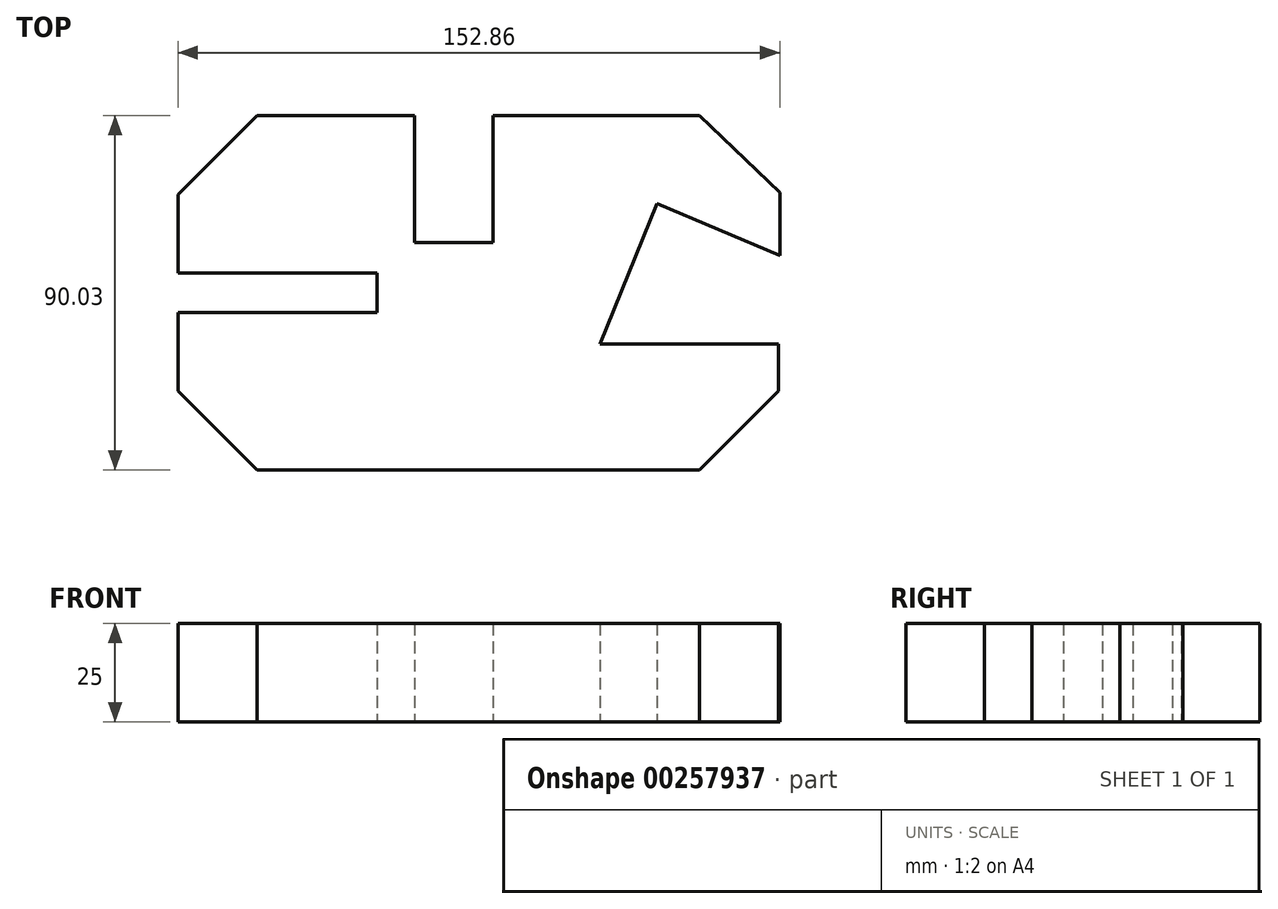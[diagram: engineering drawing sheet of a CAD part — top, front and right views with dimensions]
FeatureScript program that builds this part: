
annotation { "Feature Type Name" : "Feature", "Feature Type Description" : "" }
export const myFeature = defineFeature(function(context is Context, id is Id, definition is map)
    precondition{}
    {
        {
            var Q0;
            Q0=qCreatedBy(makeId("Top.planeOp"),FACE);
            var sketch = newSketch(context, id + "F0", { "sketchPlane" : qUnion([Q0])});
            skLineSegment(sketch, "E0", {"start": v(-83.7, -71.77) * mm, "end": v(28.8, -71.77) * mm});
            skLineSegment(sketch, "E1", {"start": v(-83.7, -71.77) * mm, "end": v(-103.7, -51.76) * mm});
            skLineSegment(sketch, "E2", {"start": v(28.8, -71.77) * mm, "end": v(48.82, -51.76) * mm});
            skLineSegment(sketch, "E3", {"start": v(-103.7, -51.76) * mm, "end": v(-103.7, -31.76) * mm});
            skLineSegment(sketch, "E4", {"start": v(48.82, -51.76) * mm, "end": v(48.82, -39.76) * mm});
            skLineSegment(sketch, "E5", {"start": v(48.82, -39.76) * mm, "end": v(3.52, -39.76) * mm});
            skLineSegment(sketch, "E6", {"start": v(-103.7, -31.76) * mm, "end": v(-53.2, -31.76) * mm});
            skLineSegment(sketch, "E7", {"start": v(-53.2, -31.76) * mm, "end": v(-53.2, -21.76) * mm});
            skLineSegment(sketch, "E8", {"start": v(-53.2, -21.76) * mm, "end": v(-103.7, -21.76) * mm});
            skLineSegment(sketch, "E9", {"start": v(-103.7, -21.76) * mm, "end": v(-103.7, -1.76) * mm});
            skLineSegment(sketch, "E10", {"start": v(-103.7, -1.76) * mm, "end": v(-83.7, 18.26) * mm});
            skLineSegment(sketch, "E11", {"start": v(-83.7, 18.26) * mm, "end": v(-43.7, 18.26) * mm});
            skLineSegment(sketch, "E12", {"start": v(-43.7, 18.26) * mm, "end": v(-43.7, -14.04) * mm});
            skLineSegment(sketch, "E13", {"start": v(-43.7, -14.04) * mm, "end": v(-23.7, -14.04) * mm});
            skLineSegment(sketch, "E14", {"start": v(-23.7, -14.04) * mm, "end": v(-23.7, 18.26) * mm});
            skLineSegment(sketch, "E15", {"start": v(-23.7, 18.26) * mm, "end": v(28.7, 18.26) * mm});
            skLineSegment(sketch, "E16", {"start": v(28.7, 18.26) * mm, "end": v(49.15, -1.3) * mm});
            skLineSegment(sketch, "E17", {"start": v(49.15, -1.3) * mm, "end": v(49.15, -17.3) * mm});
            skLineSegment(sketch, "E18", {"start": v(3.52, -39.76) * mm, "end": v(17.94, -4.06) * mm});
            skLineSegment(sketch, "E19", {"start": v(17.94, -4.06) * mm, "end": v(49.15, -17.3) * mm});
            skSolve(sketch);
        }
        {
            var Q0;
            Q0 = qSketchRegion(id + "F0", true);
            extrude(context, id + "F1", {"entities" : qUnion([Q0]), "depth" : 25 * mm});
        }
    });
